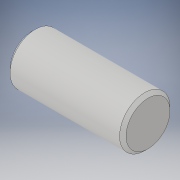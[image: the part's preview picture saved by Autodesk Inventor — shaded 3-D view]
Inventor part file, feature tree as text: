
AUTODESK INVENTOR PART (.ipt)
format: ipt  version: 2018.3 (Build 223284000, 284)  size: 100,352 bytes
history: native  units: in
note: dims shown in document units (in); Inventor stores cm internally (conversion verified against a paired STEP export)
features: revolve x1, chamfer x1, sketch x1
ambient origin geometry x8: Origin, YZ Plane, XZ Plane, XY Plane, X Axis, Y Axis, Z Axis, Center Point
bodies: Solid1 (feature_tree)
feature tree (3):
  revolve  "Revolution1"  Angle=90.0deg
  chamfer  "Chamfer1"  Distance=0.01in Angle=45.0deg
  sketch  "Sketch1"  dims[d0=0.358in d2=90.0deg d3=0.01in d4=0.125in d5=45.0deg]
